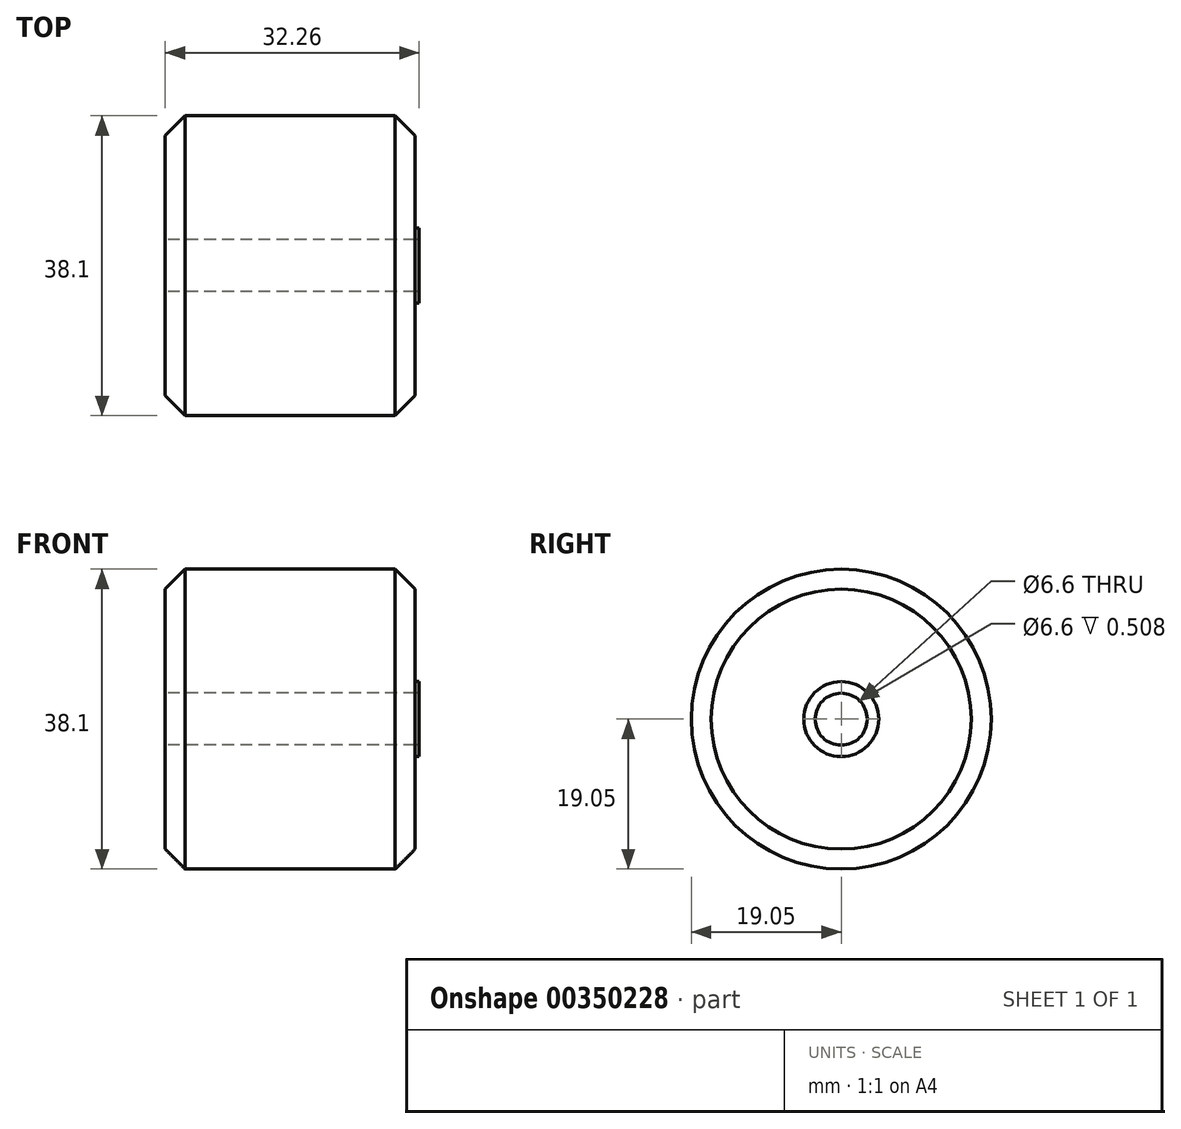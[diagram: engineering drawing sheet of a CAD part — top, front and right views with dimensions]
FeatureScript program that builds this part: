
annotation { "Feature Type Name" : "Feature", "Feature Type Description" : "" }
export const myFeature = defineFeature(function(context is Context, id is Id, definition is map)
    precondition{}
    {
        {
            var Q0;
            Q0=qCreatedBy(makeId("Right.planeOp"),FACE);
            var sketch = newSketch(context, id + "F0", { "sketchPlane" : qUnion([Q0])});
            skCircle(sketch, "E0", {"center": v(0, 0) * mm, "radius": 19.05 * mm});
            skSolve(sketch);
        }
        {
            var Q0;
            Q0=makeQuery(id+"F0.imprint","IMPRINT",FACE,{"disambiguationData":[TD([[makeQuery(id+"F0.imprint","IMPRINT",EDGE,{"derivedFrom":sQuery(id+"F0.wireOp",EDGE,"E0")}),1.0]])]});
            extrude(context, id + "F1", {"entities" : qUnion([Q0]), "depth" : 31.75 * mm});
        }
        {
            var Q0;
            Q0=qCreatedBy(makeId("Right.planeOp"),FACE);
            var sketch = newSketch(context, id + "F2", { "sketchPlane" : qUnion([Q0])});
            skCircle(sketch, "E1", {"center": v(0, 0) * mm, "radius": 3.3 * mm});
            skSolve(sketch);
        }
        {
            var Q0;
            Q0=makeQuery(id+"F2.imprint","IMPRINT",FACE,{"disambiguationData":[TD([[makeQuery(id+"F2.imprint","IMPRINT",EDGE,{"derivedFrom":sQuery(id+"F2.wireOp",EDGE,"E1")}),1.0]])]});
            extrude(context, id + "F3", {"entities" : qUnion([Q0]), "operationType" : NewBodyOperationType.REMOVE, "depth" : 31.75 * mm});
        }
        {
            var Q0;
            Q0=makeQuery(id+"F1.opExtrude","CAP_EDGE",EDGE,{"disambiguationData":[OSD([sQuery(id+"F0.wireOp",EDGE,"E0")])],"isStart":false});
            var Q1;
            Q1=makeQuery(id+"F1.opExtrude","CAP_EDGE",EDGE,{"disambiguationData":[OSD([sQuery(id+"F0.wireOp",EDGE,"E0")])],"isStart":true});
            chamfer(context, id + "F4", {"entities" : qUnion([Q0, Q1]), "width" : 2.54 * mm, "tangentPropagation" : true});
        }
        {
            var Q0;
            Q0=makeQuery(id+"F1.opExtrude","CAP_FACE",FACE,{"disambiguationData":[OSD([sQuery(id+"F0.wireOp",EDGE,"E0")])],"isStart":false});
            var sketch = newSketch(context, id + "F5", { "sketchPlane" : qUnion([Q0])});
            skCircle(sketch, "E2", {"center": v(0, 0) * mm, "radius": 4.76 * mm});
            skSolve(sketch);
        }
        {
            var Q0;
            Q0=makeQuery(id+"F5.imprint","IMPRINT",FACE,{"disambiguationData":[TD([[makeQuery(id+"F5.imprint","IMPRINT",EDGE,{"derivedFrom":sQuery(id+"F5.wireOp",EDGE,"E2")}),1.0]])]});
            extrude(context, id + "F6", {"entities" : qUnion([Q0]), "depth" : 0.5 * mm});
        }
    });
